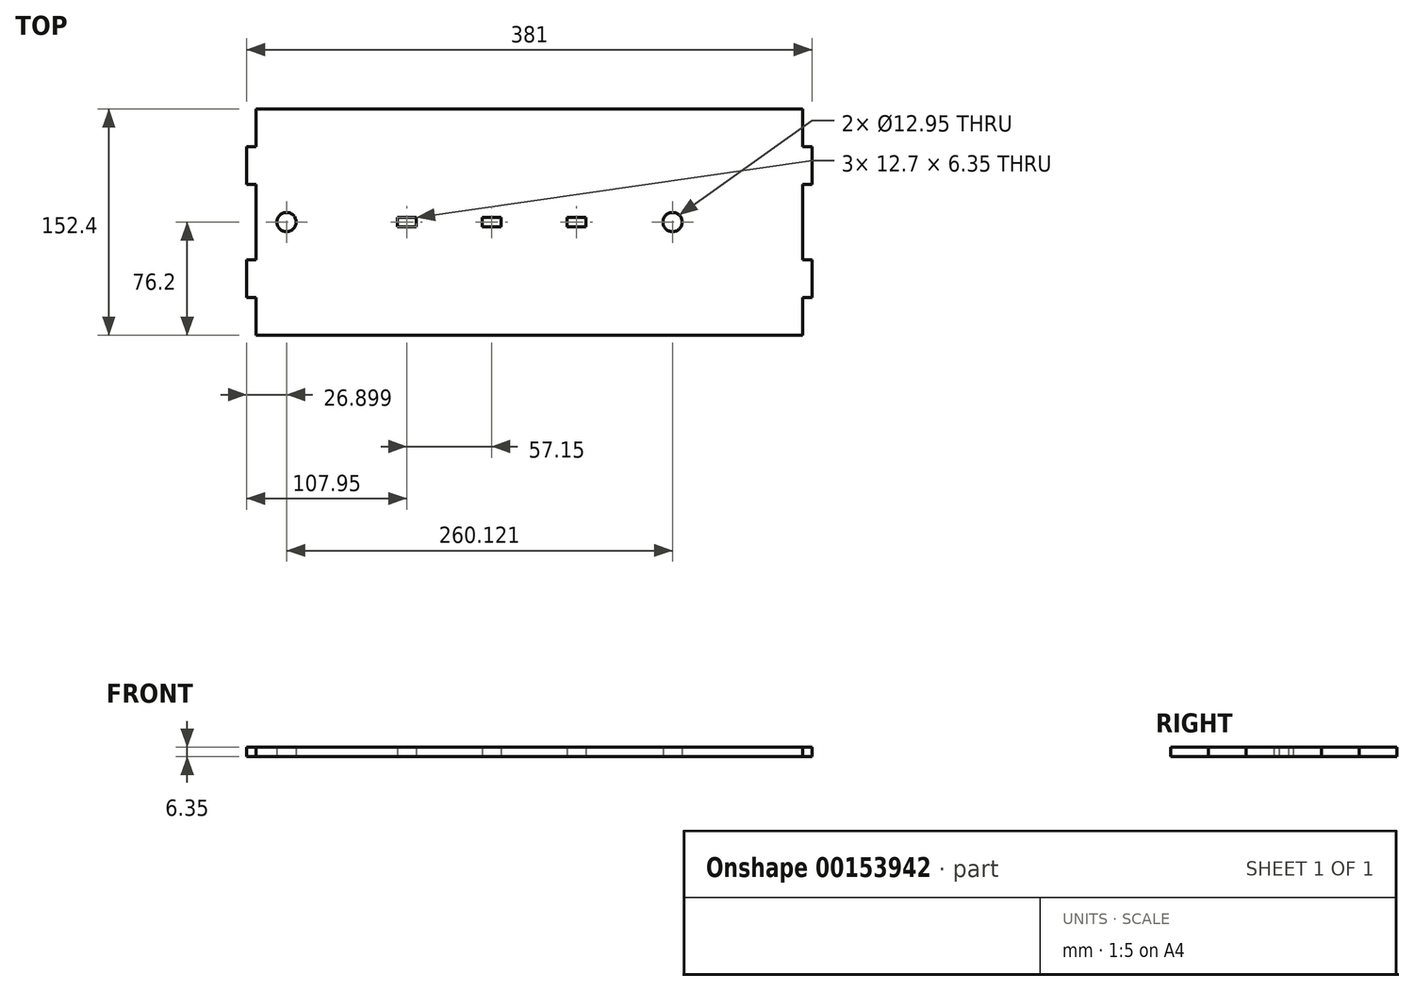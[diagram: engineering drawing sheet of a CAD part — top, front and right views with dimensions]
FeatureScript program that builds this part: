
annotation { "Feature Type Name" : "Feature", "Feature Type Description" : "" }
export const myFeature = defineFeature(function(context is Context, id is Id, definition is map)
    precondition{}
    {
        {
            var Q0;
            Q0=qCreatedBy(makeId("Top.planeOp"),FACE);
            var sketch = newSketch(context, id + "F0", { "sketchPlane" : qUnion([Q0])});
            skLineSegment(sketch, "E0.bottom", {"start": v(-184.15, 76.2) * mm, "end": v(184.15, 76.2) * mm});
            skLineSegment(sketch, "E0.top", {"start": v(-184.15, -76.2) * mm, "end": v(184.15, -76.2) * mm});
            skLineSegment(sketch, "E0.left", {"start": v(-184.15, 76.2) * mm, "end": v(-184.15, -76.2) * mm});
            skLineSegment(sketch, "E0.right", {"start": v(184.15, 76.2) * mm, "end": v(184.15, -76.2) * mm});
            skLineSegment(sketch, "E1", {"start": v(-184.15, 76.2) * mm, "end": v(-184.15, 0) * mm});
            skLineSegment(sketch, "E2", {"start": v(184.15, 76.2) * mm, "end": v(184.15, 0) * mm});
            skLineSegment(sketch, "E3", {"start": v(-184.15, 0) * mm, "end": v(184.15, 0) * mm, "construction": true});
            skCircle(sketch, "E4", {"center": v(-163.6, 0) * mm, "radius": 6.48 * mm});
            skLineSegment(sketch, "E5", {"start": v(-184.15, 0) * mm, "end": v(-107.95, 0) * mm});
            skLineSegment(sketch, "E6", {"start": v(-107.95, 0) * mm, "end": v(57.15, 0) * mm});
            skCircle(sketch, "E7", {"center": v(96.52, 0) * mm, "radius": 6.48 * mm});
            skLineSegment(sketch, "E8", {"start": v(-107.95, 0) * mm, "end": v(-88.9, 0) * mm});
            skLineSegment(sketch, "E9", {"start": v(-88.9, 0) * mm, "end": v(-88.9, 3.17) * mm});
            skLineSegment(sketch, "E10.bottom", {"start": v(-88.9, 3.17) * mm, "end": v(-76.2, 3.17) * mm});
            skLineSegment(sketch, "E10.top", {"start": v(-88.9, -3.18) * mm, "end": v(-76.2, -3.18) * mm});
            skLineSegment(sketch, "E10.left", {"start": v(-88.9, 3.17) * mm, "end": v(-88.9, -3.18) * mm});
            skLineSegment(sketch, "E10.right", {"start": v(-76.2, 3.17) * mm, "end": v(-76.2, -3.18) * mm});
            skLineSegment(sketch, "E11", {"start": v(-76.2, 3.17) * mm, "end": v(-76.2, 0) * mm});
            skLineSegment(sketch, "E12", {"start": v(-76.2, 0) * mm, "end": v(-31.75, 0) * mm});
            skLineSegment(sketch, "E13", {"start": v(-31.75, 0) * mm, "end": v(-31.75, 3.17) * mm});
            skLineSegment(sketch, "E14.bottom", {"start": v(-31.75, 3.17) * mm, "end": v(-19.05, 3.17) * mm});
            skLineSegment(sketch, "E14.top", {"start": v(-31.75, -3.18) * mm, "end": v(-19.05, -3.18) * mm});
            skLineSegment(sketch, "E14.left", {"start": v(-31.75, 3.17) * mm, "end": v(-31.75, -3.18) * mm});
            skLineSegment(sketch, "E14.right", {"start": v(-19.05, 3.17) * mm, "end": v(-19.05, -3.18) * mm});
            skLineSegment(sketch, "E15", {"start": v(-19.05, 3.17) * mm, "end": v(-19.05, 0) * mm});
            skLineSegment(sketch, "E16", {"start": v(-19.05, 0) * mm, "end": v(25.4, 0) * mm});
            skLineSegment(sketch, "E17", {"start": v(25.4, 0) * mm, "end": v(25.4, 3.17) * mm});
            skLineSegment(sketch, "E18.bottom", {"start": v(25.4, 3.17) * mm, "end": v(38.1, 3.17) * mm});
            skLineSegment(sketch, "E18.top", {"start": v(25.4, -3.18) * mm, "end": v(38.1, -3.18) * mm});
            skLineSegment(sketch, "E18.left", {"start": v(25.4, 3.17) * mm, "end": v(25.4, -3.18) * mm});
            skLineSegment(sketch, "E18.right", {"start": v(38.1, 3.17) * mm, "end": v(38.1, -3.18) * mm});
            skLineSegment(sketch, "E19", {"start": v(38.1, 3.17) * mm, "end": v(38.1, 0) * mm});
            skLineSegment(sketch, "E20", {"start": v(184.15, -76.2) * mm, "end": v(184.15, -50.8) * mm});
            skLineSegment(sketch, "E21.bottom", {"start": v(184.15, -50.8) * mm, "end": v(190.5, -50.8) * mm});
            skLineSegment(sketch, "E21.top", {"start": v(184.15, -25.4) * mm, "end": v(190.5, -25.4) * mm});
            skLineSegment(sketch, "E21.left", {"start": v(184.15, -50.8) * mm, "end": v(184.15, -25.4) * mm});
            skLineSegment(sketch, "E21.right", {"start": v(190.5, -50.8) * mm, "end": v(190.5, -25.4) * mm});
            skLineSegment(sketch, "E22.MirrorCS", {"start": v(184.15, 25.4) * mm, "end": v(190.5, 25.4) * mm});
            skLineSegment(sketch, "E23.MirrorCS", {"start": v(190.5, 50.8) * mm, "end": v(190.5, 25.4) * mm});
            skLineSegment(sketch, "E24.MirrorCS", {"start": v(184.15, 50.8) * mm, "end": v(190.5, 50.8) * mm});
            skLineSegment(sketch, "E25", {"start": v(0, 0) * mm, "end": v(0, 76.2) * mm, "construction": true});
            skLineSegment(sketch, "E26.MirrorCS", {"start": v(-184.15, 50.8) * mm, "end": v(-190.5, 50.8) * mm});
            skLineSegment(sketch, "E27.MirrorCS", {"start": v(-190.5, 50.8) * mm, "end": v(-190.5, 25.4) * mm});
            skLineSegment(sketch, "E28.MirrorCS", {"start": v(-184.15, 25.4) * mm, "end": v(-190.5, 25.4) * mm});
            skLineSegment(sketch, "E29.MirrorCS", {"start": v(-184.15, -25.4) * mm, "end": v(-190.5, -25.4) * mm});
            skLineSegment(sketch, "E30.MirrorCS", {"start": v(-190.5, -50.8) * mm, "end": v(-190.5, -25.4) * mm});
            skLineSegment(sketch, "E31.MirrorCS", {"start": v(-184.15, -50.8) * mm, "end": v(-190.5, -50.8) * mm});
            skSolve(sketch);
        }
        {
            var Q0;
            {var subQ23=sQuery(id+"F0.wireOp",EDGE,"E0.bottom");Q0=makeQuery(id+"F0.imprint","IMPRINT",FACE,{"disambiguationData":[TD([[makeQuery(id+"F0.imprint","IMPRINT",EDGE,{"derivedFrom":subQ23}),-1.0]])]});}
            extrude(context, id + "F1", {"entities" : qUnion([Q0]), "depth" : 6.35 * mm});
        }
        {
            var Q0;
            Q0=makeQuery(id+"F0.imprint","IMPRINT",FACE,{"disambiguationData":[TD([[makeQuery(id+"F0.imprint","IMPRINT",EDGE,{"derivedFrom":sQuery(id+"F0.wireOp",EDGE,"E21.bottom")}),1.0]])]});
            extrude(context, id + "F2", {"entities" : qUnion([Q0]), "operationType" : NewBodyOperationType.ADD, "depth" : 6.35 * mm});
        }
        {
            var Q0;
            {var subQ0=sQuery(id+"F0.wireOp",EDGE,"E22.MirrorCS");Q0=makeQuery(id+"F0.imprint","IMPRINT",FACE,{"disambiguationData":[TD([[makeQuery(id+"F0.imprint","IMPRINT",EDGE,{"derivedFrom":subQ0}),1.0]])]});}
            extrude(context, id + "F3", {"entities" : qUnion([Q0]), "operationType" : NewBodyOperationType.ADD, "depth" : 6.35 * mm});
        }
        {
            var Q0;
            {var subQ0=sQuery(id+"F0.wireOp",EDGE,"E29.MirrorCS");Q0=makeQuery(id+"F0.imprint","IMPRINT",FACE,{"disambiguationData":[TD([[makeQuery(id+"F0.imprint","IMPRINT",EDGE,{"derivedFrom":subQ0}),1.0]])]});}
            extrude(context, id + "F4", {"entities" : qUnion([Q0]), "operationType" : NewBodyOperationType.ADD, "depth" : 6.35 * mm});
        }
        {
            var Q0;
            {var subQ0=sQuery(id+"F0.wireOp",EDGE,"E26.MirrorCS");Q0=makeQuery(id+"F0.imprint","IMPRINT",FACE,{"disambiguationData":[TD([[makeQuery(id+"F0.imprint","IMPRINT",EDGE,{"derivedFrom":subQ0}),1.0]])]});}
            extrude(context, id + "F5", {"entities" : qUnion([Q0]), "operationType" : NewBodyOperationType.ADD, "depth" : 6.35 * mm});
        }
    });
